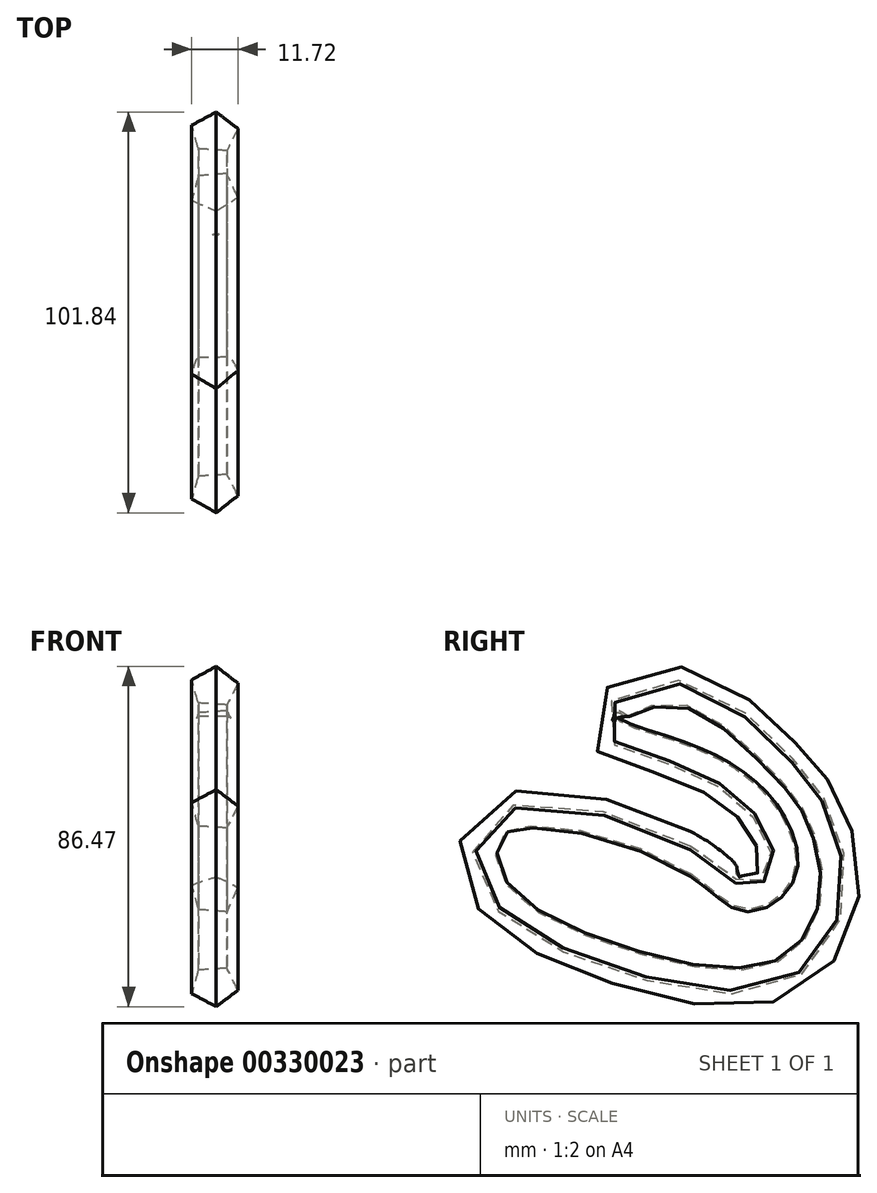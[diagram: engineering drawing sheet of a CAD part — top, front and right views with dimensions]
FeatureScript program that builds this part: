
annotation { "Feature Type Name" : "Feature", "Feature Type Description" : "" }
export const myFeature = defineFeature(function(context is Context, id is Id, definition is map)
    precondition{}
    {
        {
            var Q0;
            Q0=qCreatedBy(makeId("Front.planeOp"),FACE);
            var sketch = newSketch(context, id + "F0", { "sketchPlane" : qUnion([Q0])});
            skCircle(sketch, "E0.cCircle", {"center": v(0, 0) * mm, "radius": 5 * mm, "construction": true});
            skLineSegment(sketch, "E0.0", {"start": v(0.5, 6.16) * mm, "end": v(6.02, 1.42) * mm});
            skLineSegment(sketch, "E0.1", {"start": v(6.02, 1.42) * mm, "end": v(3.2, -5.28) * mm});
            skLineSegment(sketch, "E0.2", {"start": v(3.2, -5.28) * mm, "end": v(-4.03, -4.68) * mm});
            skLineSegment(sketch, "E0.3", {"start": v(-4.03, -4.68) * mm, "end": v(-5.7, 2.39) * mm});
            skLineSegment(sketch, "E0.4", {"start": v(-5.7, 2.39) * mm, "end": v(0.5, 6.16) * mm});
            skPoint(sketch, "E0.0.midPoint", {"position": v(3.26, 3.79) * mm});
            skSolve(sketch);
        }
        {
            var Q0;
            Q0=qCreatedBy(makeId("Right.planeOp"),FACE);
            var sketch = newSketch(context, id + "F1", { "sketchPlane" : qUnion([Q0])});
            skFitSpline(sketch, "E1", {"points": [v(0, 0) * mm, v(-47.9, 9.6) * mm, v(-51.52, -7.12) * mm, v(-19.66, -27) * mm, v(22.82, -30.84) * mm, v(37.28, -10.5) * mm, v(32.77, 12.32) * mm, v(22.37, 25.42) * mm, v(-4.97, 42.6) * mm, v(-21.47, 33.33) * mm, v(-7.46, 26.1) * mm, v(11.07, 17.29) * mm, v(20.34, 6.67) * mm, v(21.92, -4.18) * mm, v(14.69, -9.38) * mm, v(0, 0) * mm]});
            skSolve(sketch);
        }
        {
            var Q0;
            Q0=makeQuery(id+"F0.imprint","IMPRINT",FACE,{"disambiguationData":[TD([[makeQuery(id+"F0.imprint","IMPRINT",EDGE,{"derivedFrom":sQuery(id+"F0.wireOp",EDGE,"E0.0")}),-1.0]])]});
            var Q1;
            Q1=sQuery(id+"F1.wireOp",EDGE,"E1");
            sweep(context, id + "F2", {"profiles" : qUnion([Q0]), "path" : qUnion([Q1])});
        }
    });
